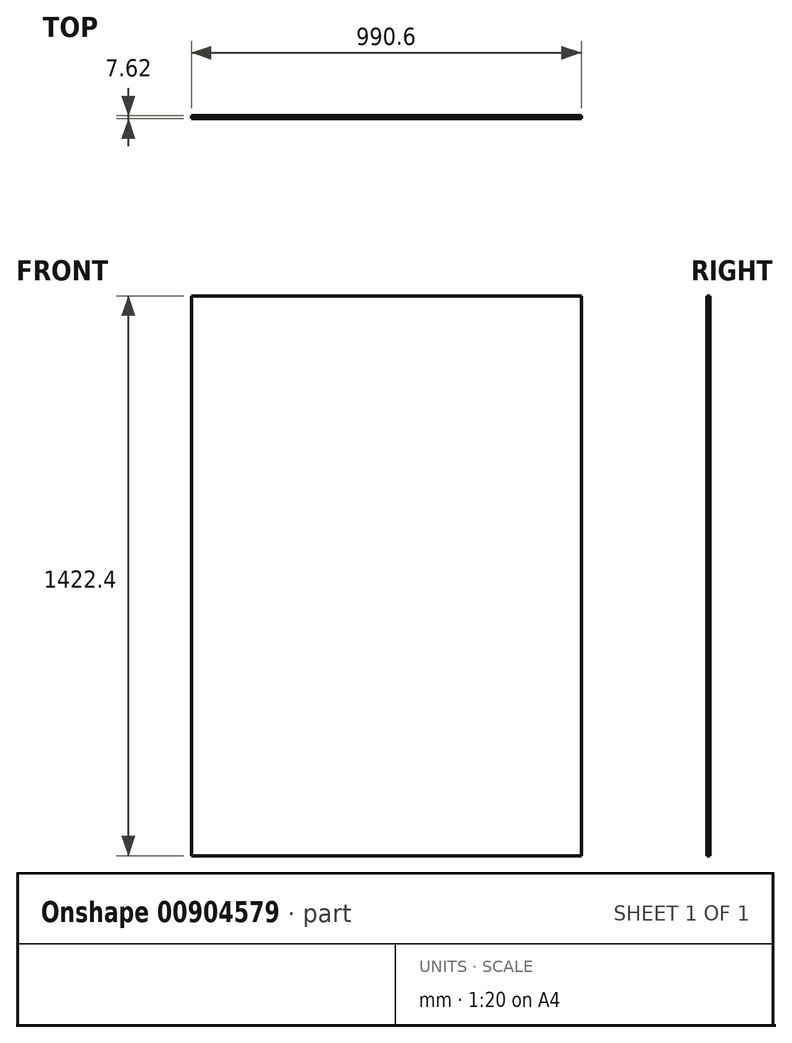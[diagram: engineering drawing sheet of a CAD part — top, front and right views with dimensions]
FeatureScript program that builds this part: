
annotation { "Feature Type Name" : "Feature", "Feature Type Description" : "" }
export const myFeature = defineFeature(function(context is Context, id is Id, definition is map)
    precondition{}
    {
        {
            var Q0;
            Q0=qCreatedBy(makeId("Front.planeOp"),FACE);
            var sketch = newSketch(context, id + "F0", { "sketchPlane" : qUnion([Q0])});
            skLineSegment(sketch, "E0.bottom", {"start": v(-495.3, 711.2) * mm, "end": v(495.3, 711.2) * mm});
            skLineSegment(sketch, "E0.top", {"start": v(-495.3, -711.2) * mm, "end": v(495.3, -711.2) * mm});
            skLineSegment(sketch, "E0.left", {"start": v(-495.3, 711.2) * mm, "end": v(-495.3, -711.2) * mm});
            skLineSegment(sketch, "E0.right", {"start": v(495.3, 711.2) * mm, "end": v(495.3, -711.2) * mm});
            skPoint(sketch, "E0.middle", {"position": v(0, 0) * mm});
            skSolve(sketch);
        }
        {
            var Q0;
            Q0=makeQuery(id+"F0.imprint","IMPRINT",FACE,{"disambiguationData":[TD([[makeQuery(id+"F0.imprint","IMPRINT",EDGE,{"derivedFrom":sQuery(id+"F0.wireOp",EDGE,"E0.bottom")}),-1.0]])]});
            extrude(context, id + "F1", {"entities" : qUnion([Q0]), "depth" : 7.62 * mm, "offsetDistance" : 25.4 * mm});
        }
    });
